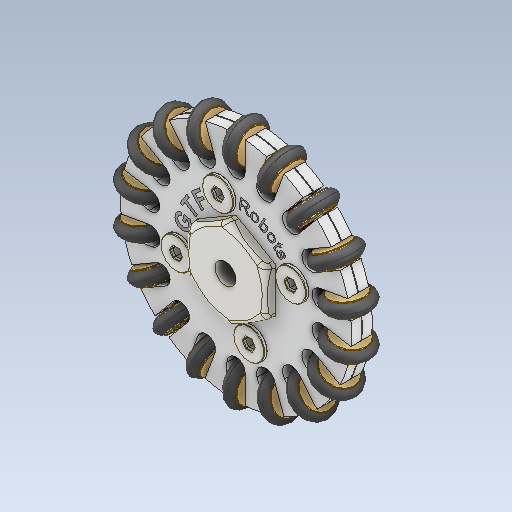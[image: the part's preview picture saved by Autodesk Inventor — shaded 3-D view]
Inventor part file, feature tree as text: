
AUTODESK INVENTOR PART (.ipt)
format: ipt  version: 2020 (Build 240168000, 168)  size: 3,832,832 bytes
history: native  units: mm
features: other x89, extrude x1, sketch x1
ambient origin geometry x8: Origin, YZ Plane, XZ Plane, XY Plane, X Axis, Y Axis, Z Axis, Center Point
bodies: Body2 (feature_tree), Body1 (feature_tree), Body3 (feature_tree), Body4 (feature_tree), Body5 (feature_tree), Body6 (feature_tree), Body7 (feature_tree), Body8 (feature_tree), Body9 (feature_tree), Body10 (feature_tree), Body11 (feature_tree), Body12 (feature_tree), Body13 (feature_tree), Body14 (feature_tree), Body15 (feature_tree), Body16 (feature_tree), Body17 (feature_tree), Body18 (feature_tree), Body19 (feature_tree), Body20 (feature_tree), Body21 (feature_tree), Body22 (feature_tree), Body23 (feature_tree), Body24 (feature_tree), Body25 (feature_tree), Body26 (feature_tree), Body27 (feature_tree), Body28 (feature_tree), Body29 (feature_tree), Body30 (feature_tree), Body31 (feature_tree), Body32 (feature_tree), Body33 (feature_tree), Body34 (feature_tree), Body35 (feature_tree), Body36 (feature_tree), Body37 (feature_tree), Body38 (feature_tree), Body39 (feature_tree), Body40 (feature_tree), Body41 (feature_tree), Body42 (feature_tree), Body43 (feature_tree), Body44 (feature_tree), Body45 (feature_tree), Body46 (feature_tree), Body47 (feature_tree), Body48 (feature_tree), Body49 (feature_tree), Body50 (feature_tree), Body51 (feature_tree), Body52 (feature_tree), Body53 (feature_tree), Body54 (feature_tree), Body55 (feature_tree), Body56 (feature_tree), Body57 (feature_tree), Body58 (feature_tree), Body59 (feature_tree), Body60 (feature_tree), Body61 (feature_tree), Body62 (feature_tree), Body63 (feature_tree), Body64 (feature_tree), Body65 (feature_tree), Body66 (feature_tree), Body67 (feature_tree), Body68 (feature_tree), Body69 (feature_tree), Body70 (feature_tree), Body71 (feature_tree), Body72 (feature_tree), Body73 (feature_tree), Body74 (feature_tree), Body75 (feature_tree), Body76 (feature_tree), Body77 (feature_tree), Body78 (feature_tree), Body79 (feature_tree), Body88 (feature_tree), Body89 (feature_tree), Body90 (feature_tree), Body91 (feature_tree), Body92 (feature_tree), Body93 (feature_tree), Body94 (feature_tree), Body95 (feature_tree), Body96 (feature_tree), Body97 (feature_tree)
feature tree (91):
  other  "Твердое тело1"
  extrude  "Выдавливание1"  Depth=4.0mm
  other  "Твердое тело2"
  other  "Твердое тело3"
  other  "Твердое тело4"
  other  "Твердое тело5"
  other  "Твердое тело6"
  other  "Твердое тело7"
  other  "Твердое тело8"
  other  "Твердое тело9"
  other  "Твердое тело10"
  other  "Твердое тело11"
  other  "Твердое тело12"
  other  "Твердое тело13"
  other  "Твердое тело14"
  other  "Твердое тело15"
  other  "Твердое тело16"
  other  "Твердое тело17"
  other  "Твердое тело18"
  other  "Твердое тело19"
  other  "Твердое тело20"
  other  "Твердое тело21"
  other  "Твердое тело22"
  other  "Твердое тело23"
  other  "Твердое тело24"
  other  "Твердое тело25"
  other  "Твердое тело26"
  other  "Твердое тело27"
  other  "Твердое тело28"
  other  "Твердое тело29"
  other  "Твердое тело30"
  other  "Твердое тело31"
  other  "Твердое тело32"
  other  "Твердое тело33"
  other  "Твердое тело34"
  other  "Твердое тело35"
  other  "Твердое тело36"
  other  "Твердое тело37"
  other  "Твердое тело38"
  other  "Твердое тело39"
  other  "Твердое тело40"
  other  "Твердое тело41"
  other  "Твердое тело42"
  other  "Твердое тело43"
  other  "Твердое тело44"
  other  "Твердое тело45"
  other  "Твердое тело46"
  other  "Твердое тело47"
  other  "Твердое тело48"
  other  "Твердое тело49"
  other  "Твердое тело50"
  other  "Твердое тело51"
  other  "Твердое тело52"
  other  "Твердое тело53"
  other  "Твердое тело54"
  other  "Твердое тело55"
  other  "Твердое тело56"
  other  "Твердое тело57"
  other  "Твердое тело58"
  other  "Твердое тело59"
  other  "Твердое тело60"
  other  "Твердое тело61"
  other  "Твердое тело62"
  other  "Твердое тело63"
  other  "Твердое тело64"
  other  "Твердое тело65"
  other  "Твердое тело66"
  other  "Твердое тело67"
  other  "Твердое тело68"
  other  "Твердое тело69"
  other  "Твердое тело70"
  other  "Твердое тело71"
  other  "Твердое тело72"
  other  "Твердое тело73"
  other  "Твердое тело74"
  other  "Твердое тело75"
  other  "Твердое тело76"
  other  "Твердое тело77"
  other  "Твердое тело78"
  other  "Твердое тело79"
  other  "Твердое тело80"
  other  "Твердое тело81"
  other  "Твердое тело82"
  other  "Твердое тело83"
  other  "Твердое тело84"
  other  "Твердое тело85"
  other  "Твердое тело86"
  other  "Твердое тело87"
  other  "Твердое тело88"
  other  "Твердое тело89"
  sketch  "Эскиз2"
